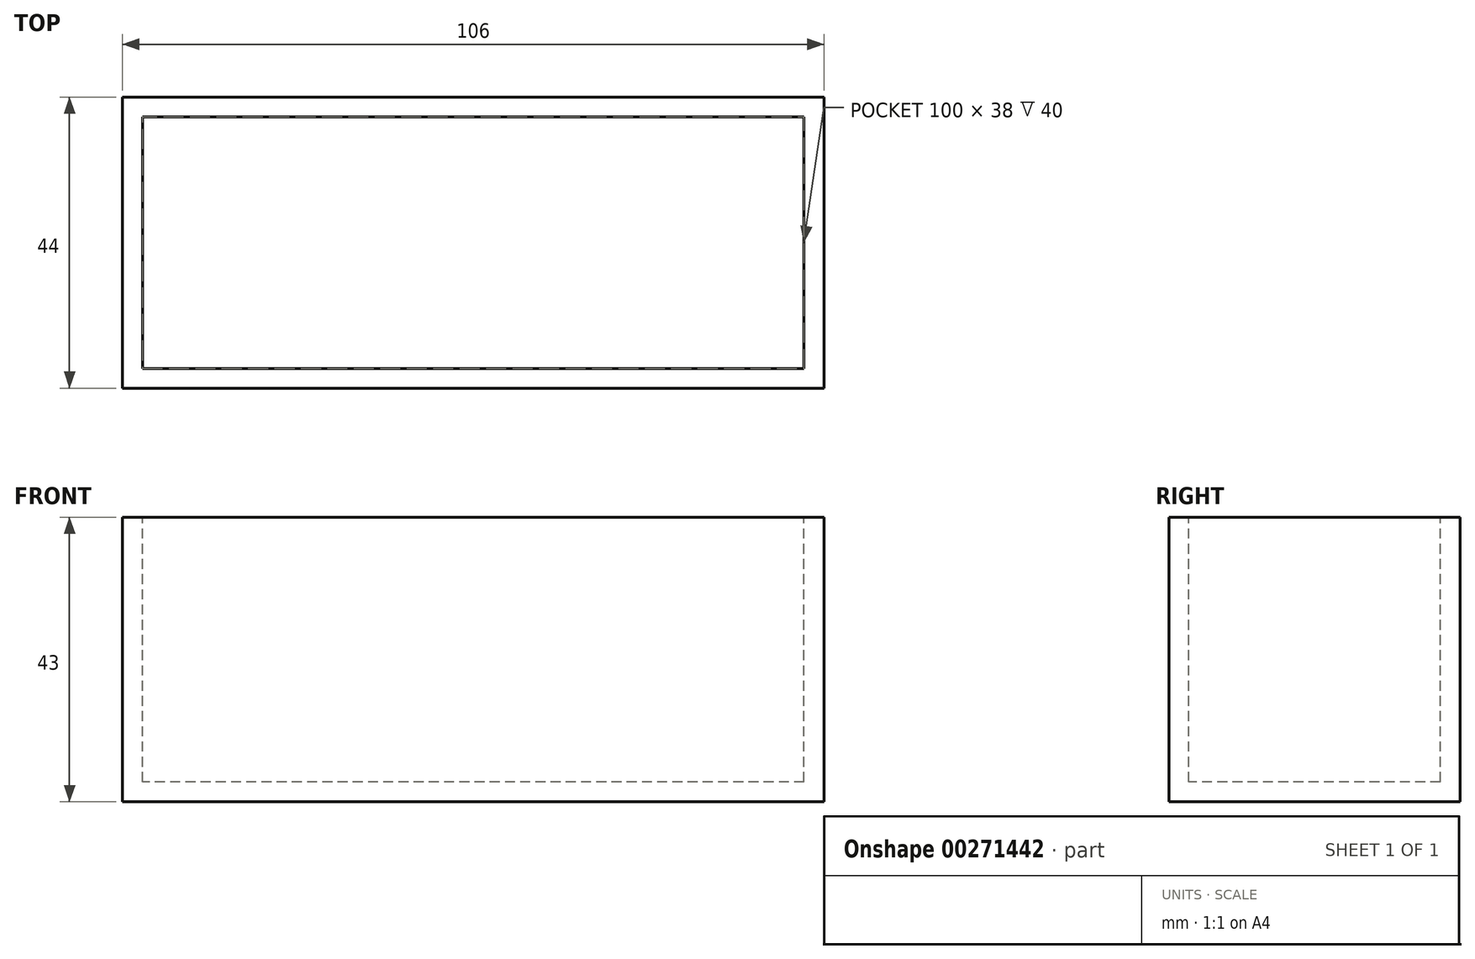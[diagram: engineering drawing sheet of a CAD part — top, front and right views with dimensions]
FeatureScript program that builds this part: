
annotation { "Feature Type Name" : "Feature", "Feature Type Description" : "" }
export const myFeature = defineFeature(function(context is Context, id is Id, definition is map)
    precondition{}
    {
        {
            assignVariable(context, id + "F0", {"name" : "wall_thickness", "anyValue" : 3});
        }
        {
            var Q0;
            Q0=qCreatedBy(makeId("Top.planeOp"),FACE);
            var sketch = newSketch(context, id + "F1", { "sketchPlane" : qUnion([Q0])});
            skLineSegment(sketch, "E0.bottom", {"start": v(50, 19) * mm, "end": v(-50, 19) * mm});
            skLineSegment(sketch, "E0.top", {"start": v(50, -19) * mm, "end": v(-50, -19) * mm});
            skLineSegment(sketch, "E0.left", {"start": v(50, 19) * mm, "end": v(50, -19) * mm});
            skLineSegment(sketch, "E0.right", {"start": v(-50, 19) * mm, "end": v(-50, -19) * mm});
            skPoint(sketch, "E0.middle", {"position": v(0, 0) * mm});
            skLineSegment(sketch, "E1.0", {"start": v(53, 22) * mm, "end": v(-53, 22) * mm});
            skLineSegment(sketch, "E1.1", {"start": v(53, 22) * mm, "end": v(53, -22) * mm});
            skLineSegment(sketch, "E1.2", {"start": v(53, -22) * mm, "end": v(-53, -22) * mm});
            skLineSegment(sketch, "E1.3", {"start": v(-53, 22) * mm, "end": v(-53, -22) * mm});
            skSolve(sketch);
        }
        {
            var Q0;
            Q0=makeQuery(id+"F1.imprint","IMPRINT",FACE,{"disambiguationData":[TD([[makeQuery(id+"F1.imprint","IMPRINT",EDGE,{"derivedFrom":sQuery(id+"F1.wireOp",EDGE,"E0.bottom")}),-1.0]])]});
            extrude(context, id + "F2", {"entities" : qUnion([Q0]), "oppositeDirection" : true, "depth" : 40 * mm});
        }
        {
            var Q0;
            Q0=makeQuery(id+"F2.opExtrude","CAP_FACE",FACE,{"disambiguationData":[OSD([sQuery(id+"F1.wireOp",EDGE,"E0.bottom"),sQuery(id+"F1.wireOp",EDGE,"E0.top"),sQuery(id+"F1.wireOp",EDGE,"E0.left"),sQuery(id+"F1.wireOp",EDGE,"E0.right"),sQuery(id+"F1.wireOp",EDGE,"E1.0"),sQuery(id+"F1.wireOp",EDGE,"E1.1"),sQuery(id+"F1.wireOp",EDGE,"E1.2"),sQuery(id+"F1.wireOp",EDGE,"E1.3")])],"isStart":false});
            var sketch = newSketch(context, id + "F3", { "sketchPlane" : qUnion([Q0])});
            skLineSegment(sketch, "E2.0", {"start": v(53, -22) * mm, "end": v(-53, -22) * mm});
            skLineSegment(sketch, "E3.0", {"start": v(-53, -22) * mm, "end": v(-53, 22) * mm});
            skLineSegment(sketch, "E4.0", {"start": v(53, 22) * mm, "end": v(-53, 22) * mm});
            skLineSegment(sketch, "E5.0", {"start": v(53, -22) * mm, "end": v(53, 22) * mm});
            skSolve(sketch);
        }
        {
            var Q0;
            Q0=makeQuery(id+"F3.imprint","IMPRINT",FACE,{"disambiguationData":[TD([[makeQuery(id+"F3.imprint","IMPRINT",EDGE,{"derivedFrom":makeQuery(id+"F2.opExtrude","CAP_EDGE",EDGE,{"disambiguationData":[OSD([sQuery(id+"F1.wireOp",EDGE,"E0.bottom")])],"isStart":false})}),-1.0]])]});
            var Q1;
            Q1=makeQuery(id+"F3.imprint","IMPRINT",FACE,{"disambiguationData":[TD([[makeQuery(id+"F3.imprint","IMPRINT",EDGE,{"derivedFrom":sQuery(id+"F3.wireOp",EDGE,"E3.0")}),-1.0]])]});
            var Q2;
            Q2=sQuery(id+"F3.wireOp",EDGE,"E3.0");
            var Q3;
            Q3=sQuery(id+"F3.wireOp",EDGE,"E4.0");
            var Q4;
            Q4=sQuery(id+"F3.wireOp",EDGE,"E5.0");
            var Q5;
            Q5=sQuery(id+"F3.wireOp",EDGE,"E2.0");
            extrude(context, id + "F4", {"entities" : qUnion([Q0, Q1]), "operationType" : NewBodyOperationType.ADD, "surfaceEntities" : qUnion([Q2, Q3, Q4, Q5]), "depth" : getVariable(context, 'wall_thickness') * mm});
        }
    });
